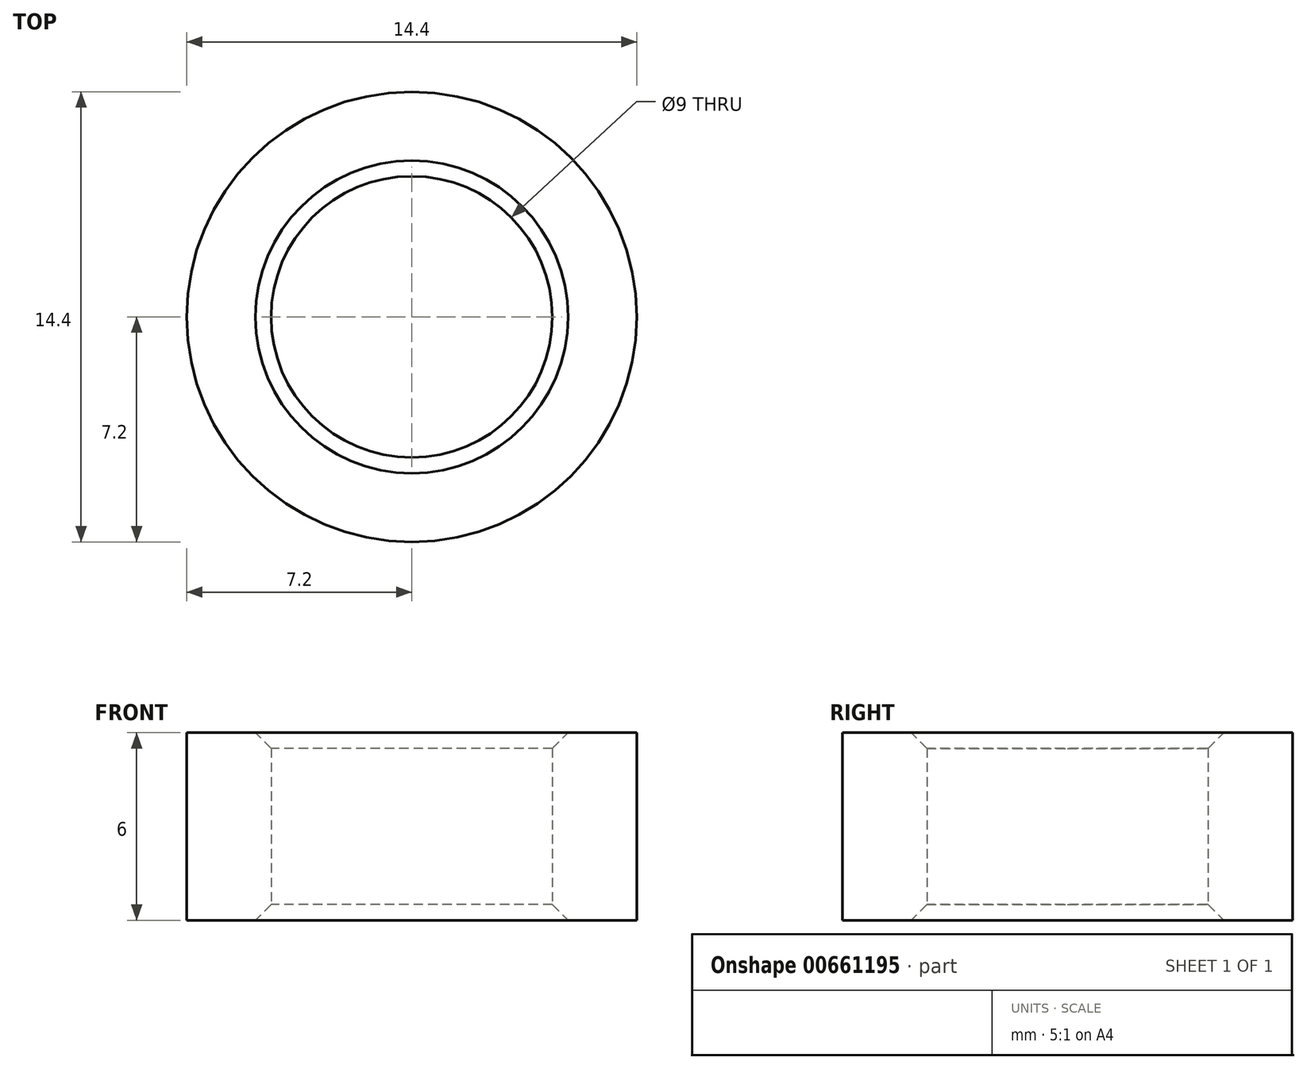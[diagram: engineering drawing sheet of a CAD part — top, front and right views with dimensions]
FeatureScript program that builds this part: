
annotation { "Feature Type Name" : "Feature", "Feature Type Description" : "" }
export const myFeature = defineFeature(function(context is Context, id is Id, definition is map)
    precondition{}
    {
        {
            var Q0;
            Q0=qCreatedBy(makeId("Top.planeOp"),FACE);
            var sketch = newSketch(context, id + "F0", { "sketchPlane" : qUnion([Q0])});
            skCircle(sketch, "E0", {"center": v(0, 0) * mm, "radius": 7.2 * mm});
            skCircle(sketch, "E1", {"center": v(0, 0) * mm, "radius": 4.5 * mm});
            skSolve(sketch);
        }
        {
            var Q0;
            Q0 = qSketchRegion(id + "F0", true);
            extrude(context, id + "F1", {"entities" : qUnion([Q0]), "depth" : 6 * mm, "offsetDistance" : 25 * mm});
        }
        {
            var Q0;
            Q0=makeQuery(id+"F1.opExtrude","CAP_EDGE",EDGE,{"disambiguationData":[OSD([sQuery(id+"F0.wireOp",EDGE,"E1")])],"isStart":false});
            chamfer(context, id + "F2", {"entities" : qUnion([Q0]), "chamferType" : ChamferType.OFFSET_ANGLE, "width" : 0.5 * mm, "oppositeDirection" : false, "angle" : 45 * degree, "tangentPropagation" : true});
        }
        {
            var Q0;
            Q0=makeQuery(id+"F1.opExtrude","CAP_EDGE",EDGE,{"disambiguationData":[OSD([sQuery(id+"F0.wireOp",EDGE,"E1")])],"isStart":true});
            chamfer(context, id + "F3", {"entities" : qUnion([Q0]), "chamferType" : ChamferType.OFFSET_ANGLE, "width" : 0.5 * mm, "oppositeDirection" : false, "angle" : 45 * degree, "tangentPropagation" : true});
        }
    });
